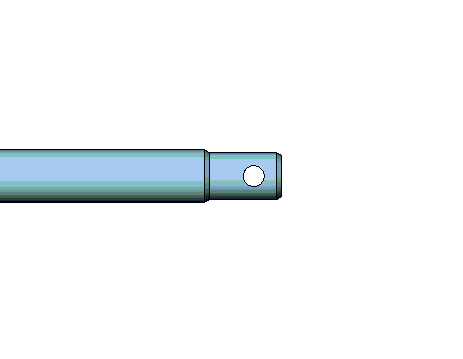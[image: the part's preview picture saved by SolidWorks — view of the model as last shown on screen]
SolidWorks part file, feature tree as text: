
SOLIDWORKS PART (.sldprt)
format: sldprt  version: not decoded by parser v0  size: 145,408 bytes
history: native  units: mm
features: plane x3, sketch x3, chamfer x3, cut_extrude x2, material x1, revolve x1 + 1 further entry (+7 scaffold rows collapsed)
feature tree (21):
  scaffold x7  (default folders/planes/origin — collapsed)
  material  "Matériau <non spécifié>"
  "Corps de surface"
  plane  "Plan1"
  plane  "Plan2"
  plane  "Plan3"
  sketch  "Esquisse1"  dims[D1=688.0mm D2=27.5mm D3=10.0mm D4=9.0mm]
  revolve  "Base-Révolution"  Angle=360deg
  chamfer  "Chanfrein1"  Distance=1mm Angle=60deg
  chamfer  "Chanfrein2"  Distance=1mm Angle=60deg
  chamfer  "Chanfrein3"  Distance=3mm Angle=30deg
  sketch  "Esquisse2"  dims[D1=8.0mm D2=10.5mm]
  cut_extrude  "Enlèv. mat.-Extru.1"  Depth=30mm
  sketch  "Esquisse3"  dims[D1=8.0mm D2=335.0mm]
  cut_extrude  "Enlèv. mat.-Extru.2"  Depth=30mm
decode coverage: 9 of 9 modeling features carry decoded parameters; 1 rows unclassified (native names shown)
note: suppression state not decoded; provenance and decode notes live in map.json
